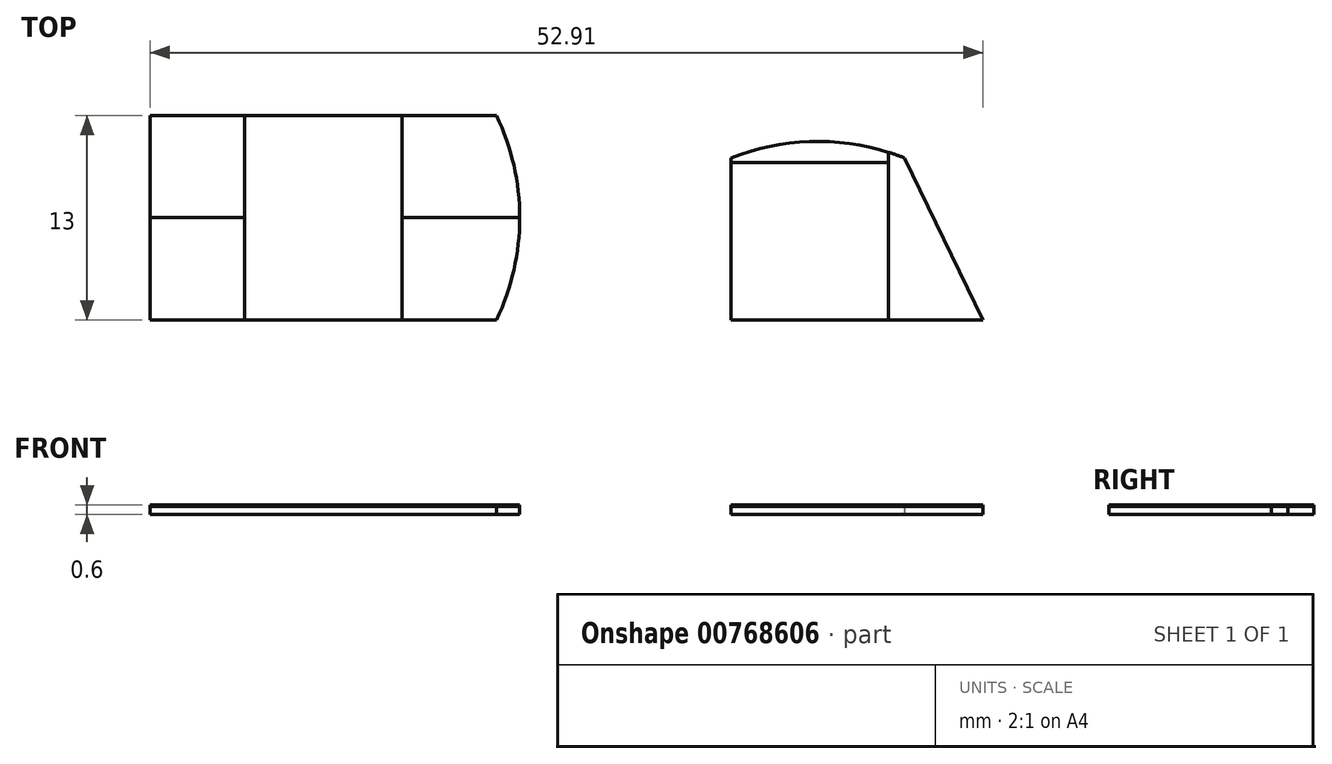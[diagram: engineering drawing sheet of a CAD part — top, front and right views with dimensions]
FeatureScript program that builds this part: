
annotation { "Feature Type Name" : "Feature", "Feature Type Description" : "" }
export const myFeature = defineFeature(function(context is Context, id is Id, definition is map)
    precondition{}
    {
        {
            var Q0;
            Q0=qCreatedBy(makeId("Top.planeOp"),FACE);
            var sketch = newSketch(context, id + "F0", { "sketchPlane" : qUnion([Q0])});
            skLineSegment(sketch, "E0.bottom", {"start": v(-26.15, 13) * mm, "end": v(-4.15, 13) * mm});
            skLineSegment(sketch, "E0.top", {"start": v(-26.15, 0) * mm, "end": v(-4.15, 0) * mm});
            skLineSegment(sketch, "E0.left", {"start": v(-26.15, 13) * mm, "end": v(-26.15, 0) * mm});
            skLineSegment(sketch, "E0.right", {"start": v(-4.15, 13) * mm, "end": v(-4.15, 0) * mm});
            skLineSegment(sketch, "E1.bottom", {"start": v(10.76, 10.3) * mm, "end": v(21.76, 10.3) * mm});
            skLineSegment(sketch, "E1.top", {"start": v(10.76, 0) * mm, "end": v(26.76, 0) * mm});
            skLineSegment(sketch, "E1.left", {"start": v(10.76, 10.3) * mm, "end": v(10.76, 0) * mm});
            skLineSegment(sketch, "E2", {"start": v(21.76, 10.3) * mm, "end": v(26.76, 0) * mm});
            skArc(sketch, "E3", {"start": v(-4.15, 0) * mm, "mid": v(-2.67, 6.5) * mm, "end": v(-4.15, 13) * mm});
            skArc(sketch, "E4", {"start": v(21.76, 10.3) * mm, "mid": v(16.26, 11.34) * mm, "end": v(10.76, 10.3) * mm});
            skSolve(sketch);
        }
        {
            var Q0;
            Q0 = qSketchRegion(id + "F0", true);
            extrude(context, id + "F1", {"entities" : qUnion([Q0]), "depth" : 0.5 * mm, "offsetDistance" : 25 * mm});
        }
        {
            var Q0;
            Q0=makeQuery(id+"F1.opExtrude","CAP_FACE",FACE,{"disambiguationData":[OSD([sQuery(id+"F0.wireOp",EDGE,"E0.bottom"),sQuery(id+"F0.wireOp",EDGE,"E0.top"),sQuery(id+"F0.wireOp",EDGE,"E0.left"),sQuery(id+"F0.wireOp",EDGE,"E3")])],"isStart":false});
            var sketch = newSketch(context, id + "F2", { "sketchPlane" : qUnion([Q0])});
            skLineSegment(sketch, "E5", {"start": v(-26.15, 6.5) * mm, "end": v(-2.67, 6.5) * mm, "construction": true});
            skLineSegment(sketch, "E6.bottom", {"start": v(-10.15, 0) * mm, "end": v(-20.15, 0) * mm});
            skLineSegment(sketch, "E6.top", {"start": v(-10.15, 13) * mm, "end": v(-20.15, 13) * mm});
            skLineSegment(sketch, "E6.left", {"start": v(-10.15, 0) * mm, "end": v(-10.15, 13) * mm});
            skLineSegment(sketch, "E6.right", {"start": v(-20.15, 0) * mm, "end": v(-20.15, 13) * mm});
            skPoint(sketch, "E6.middle", {"position": v(-15.15, 6.5) * mm});
            skLineSegment(sketch, "E7.bottom", {"start": v(-20.15, 0) * mm, "end": v(-26.15, 0) * mm});
            skLineSegment(sketch, "E7.top", {"start": v(-20.15, 13) * mm, "end": v(-26.15, 13) * mm});
            skLineSegment(sketch, "E7.right", {"start": v(-26.15, 0) * mm, "end": v(-26.15, 13) * mm});
            skPoint(sketch, "E7.middle", {"position": v(-23.15, 6.5) * mm});
            skLineSegment(sketch, "E8.bottom", {"start": v(-10.15, 0) * mm, "end": v(-2.67, 0) * mm});
            skLineSegment(sketch, "E8.top", {"start": v(-10.15, 13) * mm, "end": v(-2.67, 13) * mm});
            skLineSegment(sketch, "E8.right", {"start": v(-2.67, 0) * mm, "end": v(-2.67, 13) * mm});
            skPoint(sketch, "E8.middle", {"position": v(-6.4, 6.5) * mm});
            skLineSegment(sketch, "E9", {"start": v(-20.15, 6.5) * mm, "end": v(-26.15, 6.5) * mm});
            skLineSegment(sketch, "E10", {"start": v(-10.15, 6.5) * mm, "end": v(-2.67, 6.5) * mm});
            skSolve(sketch);
        }
        {
            var Q0;
            Q0=makeQuery(id+"F1.opExtrude","CAP_FACE",FACE,{"disambiguationData":[OSD([sQuery(id+"F0.wireOp",EDGE,"E1.top"),sQuery(id+"F0.wireOp",EDGE,"E1.left"),sQuery(id+"F0.wireOp",EDGE,"E2"),sQuery(id+"F0.wireOp",EDGE,"E4")])],"isStart":false});
            var sketch = newSketch(context, id + "F3", { "sketchPlane" : qUnion([Q0])});
            skLineSegment(sketch, "E11.bottom", {"start": v(10.76, 0) * mm, "end": v(20.76, 0) * mm});
            skLineSegment(sketch, "E11.top", {"start": v(10.76, 10) * mm, "end": v(20.76, 10) * mm});
            skLineSegment(sketch, "E11.left", {"start": v(10.76, 0) * mm, "end": v(10.76, 10) * mm});
            skLineSegment(sketch, "E11.right", {"start": v(20.76, 0) * mm, "end": v(20.76, 10) * mm});
            skLineSegment(sketch, "E12", {"start": v(20.76, 10) * mm, "end": v(20.76, 10.65) * mm});
            skSolve(sketch);
        }
        {
            var Q0;
            {var subQ0=sQuery(id+"F2.wireOp",EDGE,"E7.bottom");Q0=makeQuery(id+"F2.imprint","IMPRINT",FACE,{"disambiguationData":[TD([[makeQuery(id+"F2.imprint","IMPRINT",EDGE,{"derivedFrom":subQ0}),1.0]])]});}
            extrude(context, id + "F4", {"entities" : qUnion([Q0]), "depth" : 0.1 * mm, "offsetDistance" : 25 * mm});
        }
        {
            var Q0;
            {var subQ0=sQuery(id+"F2.wireOp",EDGE,"E7.top");Q0=makeQuery(id+"F2.imprint","IMPRINT",FACE,{"disambiguationData":[TD([[makeQuery(id+"F2.imprint","IMPRINT",EDGE,{"derivedFrom":subQ0}),-1.0]])]});}
            extrude(context, id + "F5", {"entities" : qUnion([Q0]), "depth" : 0.1 * mm, "offsetDistance" : 25 * mm});
        }
        {
            var Q0;
            {var subQ1=sQuery(id+"F2.wireOp",EDGE,"E6.bottom");Q0=makeQuery(id+"F2.imprint","IMPRINT",FACE,{"disambiguationData":[TD([[makeQuery(id+"F2.imprint","IMPRINT",EDGE,{"derivedFrom":subQ1}),1.0]])]});}
            extrude(context, id + "F6", {"entities" : qUnion([Q0]), "depth" : 0.1 * mm, "offsetDistance" : 25 * mm});
        }
        {
            var Q0;
            {var subQ5=sQuery(id+"F2.wireOp",EDGE,"E10");Q0=makeQuery(id+"F2.imprint","IMPRINT",FACE,{"disambiguationData":[TD([[makeQuery(id+"F2.imprint","IMPRINT",EDGE,{"derivedFrom":subQ5}),-1.0]])]});}
            extrude(context, id + "F7", {"entities" : qUnion([Q0]), "depth" : 0.1 * mm, "offsetDistance" : 25 * mm});
        }
        {
            var Q0;
            {var subQ5=sQuery(id+"F2.wireOp",EDGE,"E10");Q0=makeQuery(id+"F2.imprint","IMPRINT",FACE,{"disambiguationData":[TD([[makeQuery(id+"F2.imprint","IMPRINT",EDGE,{"derivedFrom":subQ5}),1.0]])]});}
            extrude(context, id + "F8", {"entities" : qUnion([Q0]), "depth" : 0.1 * mm, "offsetDistance" : 25 * mm});
        }
        {
            var Q0;
            Q0=makeQuery(id+"F3.imprint","IMPRINT",FACE,{"disambiguationData":[TD([[makeQuery(id+"F3.imprint","IMPRINT",EDGE,{"derivedFrom":sQuery(id+"F3.wireOp",EDGE,"E11.bottom")}),1.0]])]});
            extrude(context, id + "F9", {"entities" : qUnion([Q0]), "depth" : 0.1 * mm, "offsetDistance" : 25 * mm});
        }
        {
            var Q0;
            {var subQ2=sQuery(id+"F3.wireOp",EDGE,"E11.right");Q0=makeQuery(id+"F3.imprint","IMPRINT",FACE,{"disambiguationData":[TD([[makeQuery(id+"F3.imprint","IMPRINT",EDGE,{"derivedFrom":subQ2}),-1.0]])]});}
            extrude(context, id + "F10", {"entities" : qUnion([Q0]), "depth" : 0.1 * mm, "offsetDistance" : 25 * mm});
        }
        {
            var Q0;
            {var subQ0=sQuery(id+"F3.wireOp",EDGE,"E11.top");Q0=makeQuery(id+"F3.imprint","IMPRINT",FACE,{"disambiguationData":[TD([[makeQuery(id+"F3.imprint","IMPRINT",EDGE,{"derivedFrom":subQ0}),1.0]])]});}
            extrude(context, id + "F11", {"entities" : qUnion([Q0]), "depth" : 0.1 * mm, "offsetDistance" : 25 * mm});
        }
    });
